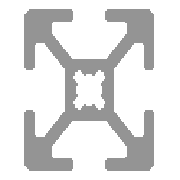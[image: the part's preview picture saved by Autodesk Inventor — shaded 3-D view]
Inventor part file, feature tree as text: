
AUTODESK INVENTOR PART (.ipt)
format: ipt  version: 2017 (Build 210142000, 142)  size: 231,936 bytes
history: native  units: in
note: dims shown in document units (in); Inventor stores cm internally (conversion verified against a paired STEP export)
features: other x2, sketch x1
ambient origin geometry x8: Origin, YZ Plane, XZ Plane, XY Plane, X Axis, Y Axis, Z Axis, Center Point
bodies: Solid1 (feature_tree), Body (feature_tree)
feature tree (3):
  other  "Blocks"
  other  "Start Plane"
  sketch  "Sketch1"  dims[d2=72.0in d4=30.0in d5=0.0in d7=1.0in]
